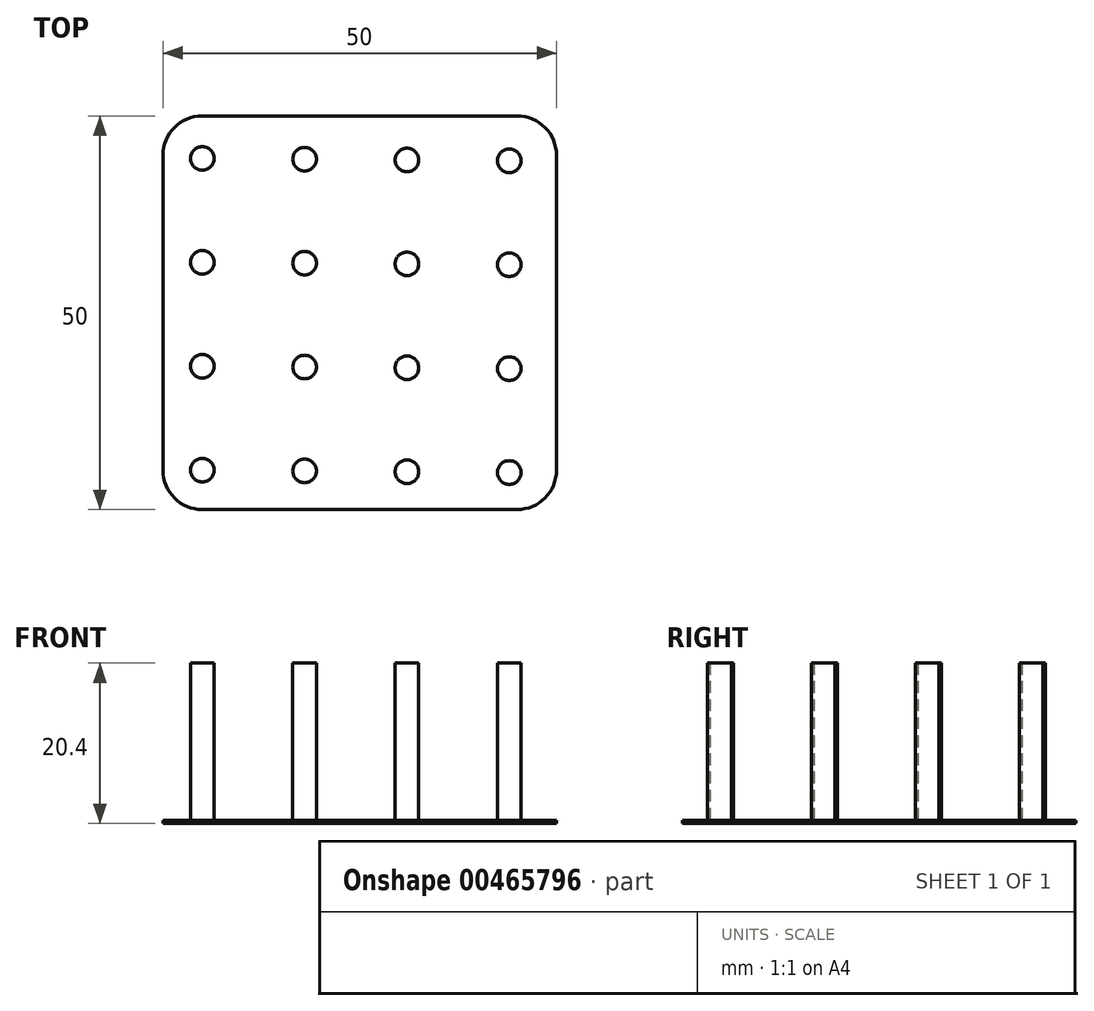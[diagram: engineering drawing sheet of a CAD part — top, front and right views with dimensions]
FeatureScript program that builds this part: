
annotation { "Feature Type Name" : "Feature", "Feature Type Description" : "" }
export const myFeature = defineFeature(function(context is Context, id is Id, definition is map)
    precondition{}
    {
        {
            var Q0;
            Q0=qCreatedBy(makeId("Top.planeOp"),FACE);
            var sketch = newSketch(context, id + "F0", { "sketchPlane" : qUnion([Q0])});
            skLineSegment(sketch, "E0.bottom", {"start": v(-20, -25) * mm, "end": v(20, -25) * mm});
            skLineSegment(sketch, "E0.top", {"start": v(-20, 25) * mm, "end": v(20, 25) * mm});
            skLineSegment(sketch, "E0.left", {"start": v(-25, -20) * mm, "end": v(-25, 20) * mm});
            skLineSegment(sketch, "E0.right", {"start": v(25, -20) * mm, "end": v(25, 20) * mm});
            skPoint(sketch, "E1.visualSharp", {"position": v(-25, 25) * mm});
            skArc(sketch, "E1.filletArc", {"start": v(-20, 25) * mm, "mid": v(-23.54, 23.54) * mm, "end": v(-25, 20) * mm});
            skPoint(sketch, "E2.visualSharp", {"position": v(25, 25) * mm});
            skArc(sketch, "E2.filletArc", {"start": v(25, 20) * mm, "mid": v(23.54, 23.54) * mm, "end": v(20, 25) * mm});
            skPoint(sketch, "E3.visualSharp", {"position": v(25, -25) * mm});
            skArc(sketch, "E3.filletArc", {"start": v(20, -25) * mm, "mid": v(23.54, -23.54) * mm, "end": v(25, -20) * mm});
            skPoint(sketch, "E4.visualSharp", {"position": v(-25, -25) * mm});
            skArc(sketch, "E4.filletArc", {"start": v(-25, -20) * mm, "mid": v(-23.54, -23.54) * mm, "end": v(-20, -25) * mm});
            skSolve(sketch);
        }
        {
            var Q0;
            Q0=makeQuery(id+"F0.imprint","IMPRINT",FACE,{"disambiguationData":[TD([[makeQuery(id+"F0.imprint","IMPRINT",EDGE,{"derivedFrom":sQuery(id+"F0.wireOp",EDGE,"E0.bottom")}),1.0]])]});
            extrude(context, id + "F1", {"entities" : qUnion([Q0]), "depth" : .4 * mm});
        }
        {
            var Q0;
            Q0=makeQuery(id+"F1.opExtrude","CAP_FACE",FACE,{"disambiguationData":[OSD([sQuery(id+"F0.wireOp",EDGE,"E0.bottom"),sQuery(id+"F0.wireOp",EDGE,"E0.top"),sQuery(id+"F0.wireOp",EDGE,"E0.left"),sQuery(id+"F0.wireOp",EDGE,"E0.right"),sQuery(id+"F0.wireOp",EDGE,"E1.filletArc"),sQuery(id+"F0.wireOp",EDGE,"E2.filletArc"),sQuery(id+"F0.wireOp",EDGE,"E3.filletArc"),sQuery(id+"F0.wireOp",EDGE,"E4.filletArc")])],"isStart":false});
            var sketch = newSketch(context, id + "F2", { "sketchPlane" : qUnion([Q0])});
            skCircle(sketch, "E5", {"center": v(-20, -20) * mm, "radius": 1.5 * mm});
            skCircle(sketch, "E6.0.1.0", {"center": v(-20, -6.8) * mm, "radius": 1.5 * mm});
            skCircle(sketch, "E6.0.2.0", {"center": v(-20, 6.4) * mm, "radius": 1.5 * mm});
            skCircle(sketch, "E6.0.3.0", {"center": v(-20, 19.6) * mm, "radius": 1.5 * mm});
            skCircle(sketch, "E6.1.0.0", {"center": v(-7, -20.1) * mm, "radius": 1.5 * mm});
            skCircle(sketch, "E6.1.1.0", {"center": v(-7, -6.9) * mm, "radius": 1.5 * mm});
            skCircle(sketch, "E6.1.2.0", {"center": v(-7, 6.3) * mm, "radius": 1.5 * mm});
            skCircle(sketch, "E6.1.3.0", {"center": v(-7, 19.5) * mm, "radius": 1.5 * mm});
            skCircle(sketch, "E6.2.0.0", {"center": v(6, -20.2) * mm, "radius": 1.5 * mm});
            skCircle(sketch, "E6.2.1.0", {"center": v(6, -7) * mm, "radius": 1.5 * mm});
            skCircle(sketch, "E6.2.2.0", {"center": v(6, 6.2) * mm, "radius": 1.5 * mm});
            skCircle(sketch, "E6.2.3.0", {"center": v(6, 19.4) * mm, "radius": 1.5 * mm});
            skCircle(sketch, "E6.3.0.0", {"center": v(19, -20.3) * mm, "radius": 1.5 * mm});
            skCircle(sketch, "E6.3.1.0", {"center": v(19, -7.1) * mm, "radius": 1.5 * mm});
            skCircle(sketch, "E6.3.2.0", {"center": v(19, 6.1) * mm, "radius": 1.5 * mm});
            skCircle(sketch, "E6.3.3.0", {"center": v(19, 19.3) * mm, "radius": 1.5 * mm});
            skLineSegment(sketch, "E6.direction1", {"start": v(-20, -20) * mm, "end": v(-7, -20.1) * mm, "construction": true});
            skLineSegment(sketch, "E6.direction2", {"start": v(-20, -20) * mm, "end": v(-20, -6.8) * mm, "construction": true});
            skSolve(sketch);
        }
        {
            var Q0;
            Q0 = qSketchRegion(id + "F2", true);
            extrude(context, id + "F3", {"entities" : qUnion([Q0]), "operationType" : NewBodyOperationType.ADD, "depth" : 20 * mm});
        }
    });
